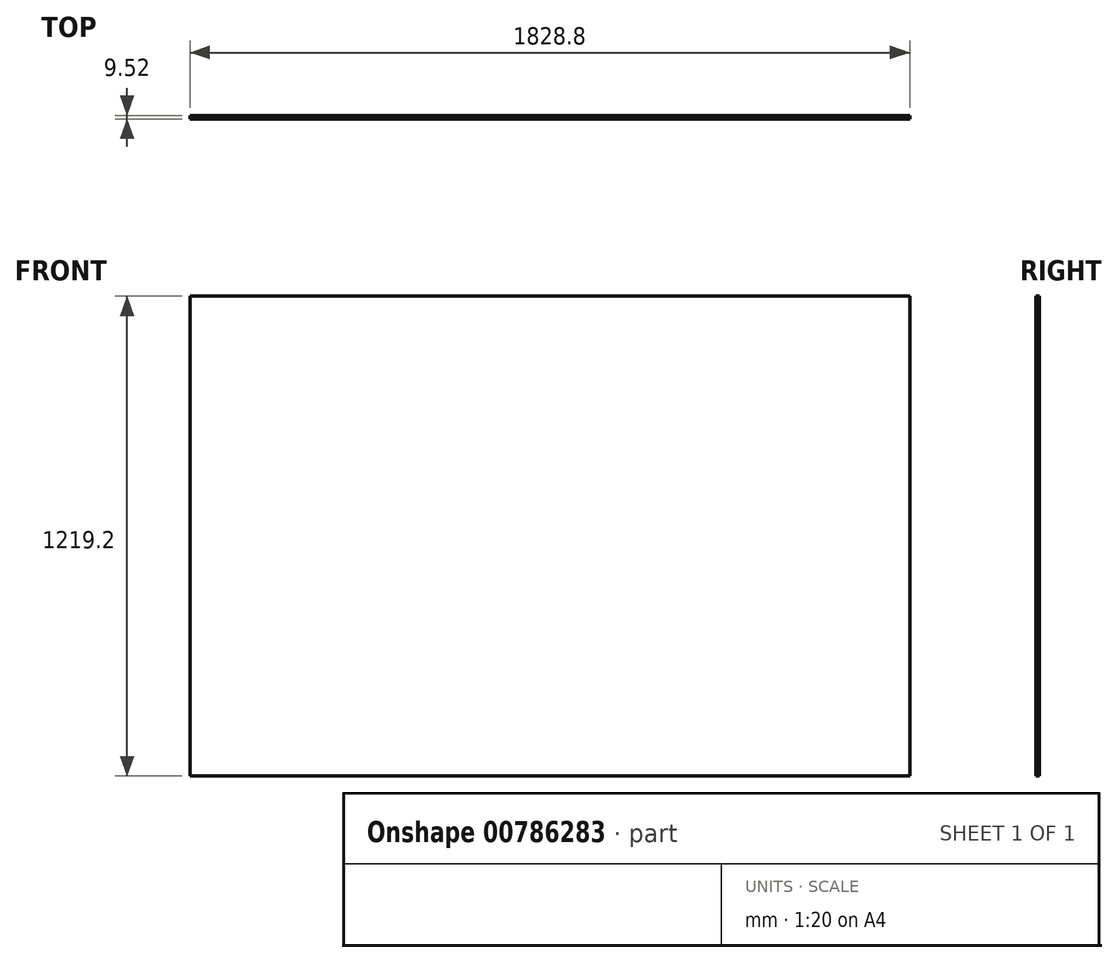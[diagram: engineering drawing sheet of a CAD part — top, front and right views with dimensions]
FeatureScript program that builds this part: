
annotation { "Feature Type Name" : "Feature", "Feature Type Description" : "" }
export const myFeature = defineFeature(function(context is Context, id is Id, definition is map)
    precondition{}
    {
        {
            var Q0;
            Q0=qCreatedBy(makeId("Front.planeOp"),FACE);
            var sketch = newSketch(context, id + "F0", { "sketchPlane" : qUnion([Q0])});
            skLineSegment(sketch, "E0.bottom", {"start": v(-914.4, 609.6) * mm, "end": v(914.4, 609.6) * mm});
            skLineSegment(sketch, "E0.top", {"start": v(-914.4, -609.6) * mm, "end": v(914.4, -609.6) * mm});
            skLineSegment(sketch, "E0.left", {"start": v(-914.4, 609.6) * mm, "end": v(-914.4, -609.6) * mm});
            skLineSegment(sketch, "E0.right", {"start": v(914.4, 609.6) * mm, "end": v(914.4, -609.6) * mm});
            skPoint(sketch, "E0.middle", {"position": v(0, 0) * mm});
            skSolve(sketch);
        }
        {
            var Q0;
            Q0=makeQuery(id+"F0.imprint","IMPRINT",FACE,{"disambiguationData":[TD([[makeQuery(id+"F0.imprint","IMPRINT",EDGE,{"derivedFrom":sQuery(id+"F0.wireOp",EDGE,"E0.bottom")}),-1.0]])]});
            extrude(context, id + "F1", {"entities" : qUnion([Q0]), "endBound" : BoundingType.SYMMETRIC, "depth" : 9.52 * mm, "offsetDistance" : 25.4 * mm});
        }
    });
